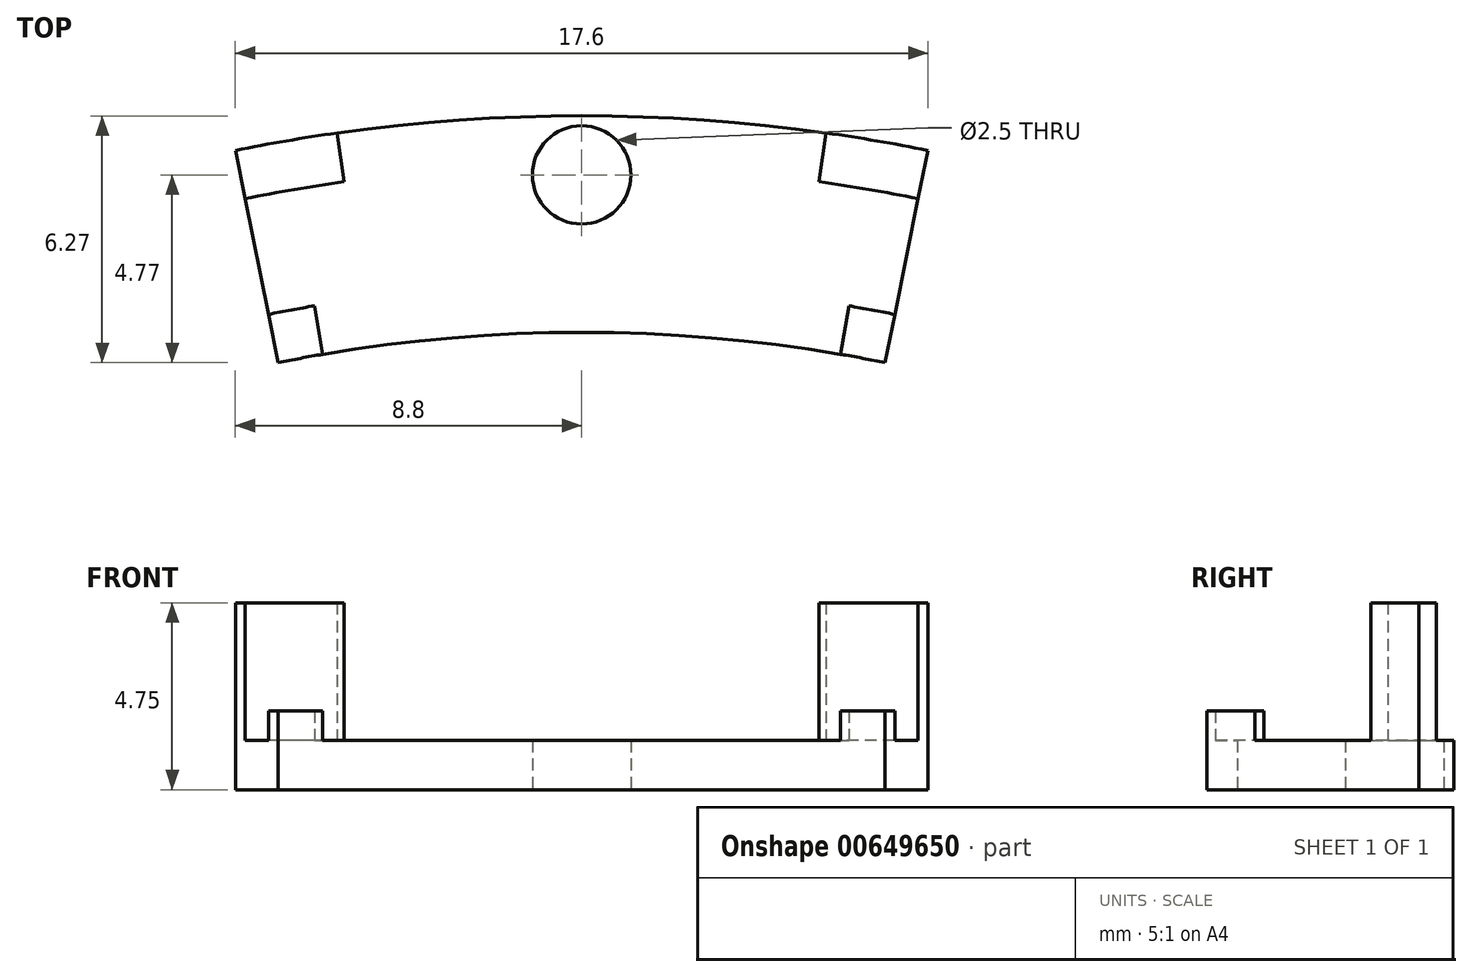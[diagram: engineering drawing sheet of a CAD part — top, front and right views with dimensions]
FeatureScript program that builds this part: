
annotation { "Feature Type Name" : "Feature", "Feature Type Description" : "" }
export const myFeature = defineFeature(function(context is Context, id is Id, definition is map)
    precondition{}
    {
        {
            var Q0;
            Q0=qCreatedBy(makeId("Top.planeOp"),FACE);
            var sketch = newSketch(context, id + "F0", { "sketchPlane" : qUnion([Q0])});
            skCircle(sketch, "E0", {"center": v(0, 0) * mm, "radius": 39 * mm});
            skCircle(sketch, "E1", {"center": v(0, 0) * mm, "radius": 44.5 * mm});
            skCircle(sketch, "E2", {"center": v(0, 43) * mm, "radius": 1.25 * mm});
            skCircle(sketch, "E3", {"center": v(0, 43) * mm, "radius": 6 * mm});
            skLineSegment(sketch, "E4", {"start": v(-7.7, 38.23) * mm, "end": v(-8.8, 43.62) * mm});
            skLineSegment(sketch, "E5", {"start": v(7.7, 38.23) * mm, "end": v(8.8, 43.62) * mm});
            skLineSegment(sketch, "E6", {"start": v(-7.5, 43.86) * mm, "end": v(-6.58, 38.44) * mm});
            skLineSegment(sketch, "E7", {"start": v(6.58, 38.44) * mm, "end": v(7.5, 43.86) * mm});
            skCircle(sketch, "E8", {"center": v(0, 0) * mm, "radius": 40.25 * mm});
            skCircle(sketch, "E9", {"center": v(0, 0) * mm, "radius": 43.25 * mm});
            skSolve(sketch);
        }
        {
            var Q0;
            {var subQ0=sQuery(id+"F0.wireOp",EDGE,"E7");var subQ1=sQuery(id+"F0.wireOp",EDGE,"E1");var subQ2=makeQuery(id+"F0.imprint","INTERSECT",VERTEX,{"derivedFrom":[subQ1,subQ0]});Q0=makeQuery(id+"F0.imprint","IMPRINT",FACE,{"disambiguationData":[TD([[makeQuery(id+"F0.imprint","IMPRINT",EDGE,{"disambiguationData":[TD([[subQ2,-1.0]])],"derivedFrom":subQ1}),1.0]])]});}
            var Q1;
            {var subQ0=sQuery(id+"F0.wireOp",EDGE,"E6");var subQ1=sQuery(id+"F0.wireOp",EDGE,"E1");var subQ2=makeQuery(id+"F0.imprint","INTERSECT",VERTEX,{"derivedFrom":[subQ1,subQ0]});Q1=makeQuery(id+"F0.imprint","IMPRINT",FACE,{"disambiguationData":[TD([[makeQuery(id+"F0.imprint","IMPRINT",EDGE,{"disambiguationData":[TD([[subQ2,1.0]])],"derivedFrom":subQ1}),1.0]])]});}
            var Q2;
            {var subQ0=sQuery(id+"F0.wireOp",EDGE,"E3");var subQ1=sQuery(id+"F0.wireOp",EDGE,"E1");var subQ2=makeQuery(id+"F0.imprint","INTERSECT",VERTEX,{"disambiguationData":[OD(0.0)],"derivedFrom":[subQ1,subQ0]});Q2=makeQuery(id+"F0.imprint","IMPRINT",FACE,{"disambiguationData":[TD([[makeQuery(id+"F0.imprint","IMPRINT",EDGE,{"disambiguationData":[TD([[subQ2,-1.0]])],"derivedFrom":subQ1}),1.0]])]});}
            var Q3;
            {var subQ0=sQuery(id+"F0.wireOp",EDGE,"E8");var subQ1=sQuery(id+"F0.wireOp",EDGE,"E3");var subQ2=makeQuery(id+"F0.imprint","INTERSECT",VERTEX,{"disambiguationData":[OD(1.0)],"derivedFrom":[subQ1,subQ0]});Q3=makeQuery(id+"F0.imprint","IMPRINT",FACE,{"disambiguationData":[TD([[makeQuery(id+"F0.imprint","IMPRINT",EDGE,{"disambiguationData":[TD([[subQ2,-1.0]])],"derivedFrom":subQ1}),-1.0]])]});}
            var Q4;
            {var subQ3=sQuery(id+"F0.wireOp",EDGE,"E9");var subQ5=sQuery(id+"F0.wireOp",EDGE,"E2");var subQ6=makeQuery(id+"F0.imprint","INTERSECT",VERTEX,{"disambiguationData":[OD(0.0)],"derivedFrom":[subQ5,subQ3]});Q4=makeQuery(id+"F0.imprint","IMPRINT",FACE,{"disambiguationData":[TD([[makeQuery(id+"F0.imprint","IMPRINT",EDGE,{"disambiguationData":[TD([[subQ6,1.0]])],"derivedFrom":subQ5}),-1.0]])]});}
            var Q5;
            {var subQ0=sQuery(id+"F0.wireOp",EDGE,"E9");var subQ1=sQuery(id+"F0.wireOp",EDGE,"E3");var subQ2=makeQuery(id+"F0.imprint","INTERSECT",VERTEX,{"disambiguationData":[OD(0.0)],"derivedFrom":[subQ1,subQ0]});Q5=makeQuery(id+"F0.imprint","IMPRINT",FACE,{"disambiguationData":[TD([[makeQuery(id+"F0.imprint","IMPRINT",EDGE,{"disambiguationData":[TD([[subQ2,-1.0]])],"derivedFrom":subQ1}),-1.0]])]});}
            var Q6;
            {var subQ0=sQuery(id+"F0.wireOp",EDGE,"E6");var subQ1=sQuery(id+"F0.wireOp",EDGE,"E0");var subQ2=makeQuery(id+"F0.imprint","INTERSECT",VERTEX,{"derivedFrom":[subQ1,subQ0]});Q6=makeQuery(id+"F0.imprint","IMPRINT",FACE,{"disambiguationData":[TD([[makeQuery(id+"F0.imprint","IMPRINT",EDGE,{"disambiguationData":[TD([[subQ2,1.0]])],"derivedFrom":subQ1}),-1.0]])]});}
            var Q7;
            {var subQ0=sQuery(id+"F0.wireOp",EDGE,"E3");var subQ1=sQuery(id+"F0.wireOp",EDGE,"E0");var subQ2=makeQuery(id+"F0.imprint","INTERSECT",VERTEX,{"disambiguationData":[OD(0.0)],"derivedFrom":[subQ1,subQ0]});Q7=makeQuery(id+"F0.imprint","IMPRINT",FACE,{"disambiguationData":[TD([[makeQuery(id+"F0.imprint","IMPRINT",EDGE,{"disambiguationData":[TD([[subQ2,-1.0]])],"derivedFrom":subQ1}),-1.0]])]});}
            var Q8;
            {var subQ0=sQuery(id+"F0.wireOp",EDGE,"E7");var subQ1=sQuery(id+"F0.wireOp",EDGE,"E0");var subQ2=makeQuery(id+"F0.imprint","INTERSECT",VERTEX,{"derivedFrom":[subQ1,subQ0]});Q8=makeQuery(id+"F0.imprint","IMPRINT",FACE,{"disambiguationData":[TD([[makeQuery(id+"F0.imprint","IMPRINT",EDGE,{"disambiguationData":[TD([[subQ2,-1.0]])],"derivedFrom":subQ1}),-1.0]])]});}
            var Q9;
            {var subQ0=sQuery(id+"F0.wireOp",EDGE,"E8");var subQ1=sQuery(id+"F0.wireOp",EDGE,"E5");var subQ2=makeQuery(id+"F0.imprint","INTERSECT",VERTEX,{"derivedFrom":[subQ1,subQ0]});Q9=makeQuery(id+"F0.imprint","IMPRINT",FACE,{"disambiguationData":[TD([[makeQuery(id+"F0.imprint","IMPRINT",EDGE,{"disambiguationData":[TD([[subQ2,-1.0]])],"derivedFrom":subQ1}),1.0]])]});}
            var Q10;
            {var subQ0=sQuery(id+"F0.wireOp",EDGE,"E8");var subQ1=sQuery(id+"F0.wireOp",EDGE,"E4");var subQ2=makeQuery(id+"F0.imprint","INTERSECT",VERTEX,{"derivedFrom":[subQ1,subQ0]});Q10=makeQuery(id+"F0.imprint","IMPRINT",FACE,{"disambiguationData":[TD([[makeQuery(id+"F0.imprint","IMPRINT",EDGE,{"disambiguationData":[TD([[subQ2,-1.0]])],"derivedFrom":subQ1}),-1.0]])]});}
            extrude(context, id + "F1", {"entities" : qUnion([Q0, Q1, Q2, Q3, Q4, Q5, Q6, Q7, Q8, Q9, Q10]), "depth" : 1.25 * mm, "offsetDistance" : 25 * mm});
        }
        {
            var Q0;
            Q0=qCreatedBy(makeId("Top.planeOp"),FACE);
            var sketch = newSketch(context, id + "F2", { "sketchPlane" : qUnion([Q0])});
            skCircle(sketch, "E10", {"center": v(0, 0) * mm, "radius": 39 * mm});
            skCircle(sketch, "E11", {"center": v(0, 0) * mm, "radius": 44.5 * mm});
            skCircle(sketch, "E12", {"center": v(0, 43) * mm, "radius": 0.85 * mm});
            skCircle(sketch, "E13", {"center": v(0, 43) * mm, "radius": 6 * mm});
            skLineSegment(sketch, "E14", {"start": v(-7.7, 38.23) * mm, "end": v(-8.8, 43.62) * mm});
            skLineSegment(sketch, "E15", {"start": v(7.7, 38.23) * mm, "end": v(8.8, 43.62) * mm});
            skLineSegment(sketch, "E16", {"start": v(-6.2, 44.06) * mm, "end": v(-5.44, 38.62) * mm});
            skLineSegment(sketch, "E17", {"start": v(5.44, 38.62) * mm, "end": v(6.2, 44.06) * mm});
            skCircle(sketch, "E18", {"center": v(0, 0) * mm, "radius": 40.25 * mm});
            skCircle(sketch, "E19", {"center": v(0, 0) * mm, "radius": 43.25 * mm});
            skSolve(sketch);
        }
        {
            var Q0;
            {var subQ0=sQuery(id+"F2.wireOp",EDGE,"E15");var subQ1=sQuery(id+"F2.wireOp",EDGE,"E11");var subQ2=makeQuery(id+"F2.imprint","INTERSECT",VERTEX,{"derivedFrom":[subQ1,subQ0]});Q0=makeQuery(id+"F2.imprint","IMPRINT",FACE,{"disambiguationData":[TD([[makeQuery(id+"F2.imprint","IMPRINT",EDGE,{"disambiguationData":[TD([[subQ2,-1.0]])],"derivedFrom":subQ1}),1.0]])]});}
            var Q1;
            {var subQ0=sQuery(id+"F2.wireOp",EDGE,"E14");var subQ1=sQuery(id+"F2.wireOp",EDGE,"E11");var subQ2=makeQuery(id+"F2.imprint","INTERSECT",VERTEX,{"derivedFrom":[subQ1,subQ0]});Q1=makeQuery(id+"F2.imprint","IMPRINT",FACE,{"disambiguationData":[TD([[makeQuery(id+"F2.imprint","IMPRINT",EDGE,{"disambiguationData":[TD([[subQ2,1.0]])],"derivedFrom":subQ1}),1.0]])]});}
            extrude(context, id + "F3", {"entities" : qUnion([Q0, Q1]), "operationType" : NewBodyOperationType.ADD, "depth" : 4.75 * mm, "offsetDistance" : 25 * mm});
        }
        {
            var Q0;
            Q0=qCreatedBy(makeId("Top.planeOp"),FACE);
            var sketch = newSketch(context, id + "F4", { "sketchPlane" : qUnion([Q0])});
            skCircle(sketch, "E20", {"center": v(0, 0) * mm, "radius": 39 * mm});
            skCircle(sketch, "E21", {"center": v(0, 0) * mm, "radius": 44.5 * mm});
            skCircle(sketch, "E22", {"center": v(0, 43) * mm, "radius": 0.85 * mm});
            skCircle(sketch, "E23", {"center": v(0, 43) * mm, "radius": 6 * mm});
            skLineSegment(sketch, "E24", {"start": v(-7.7, 38.23) * mm, "end": v(-8.8, 43.62) * mm});
            skLineSegment(sketch, "E25", {"start": v(7.7, 38.23) * mm, "end": v(8.8, 43.62) * mm});
            skLineSegment(sketch, "E26", {"start": v(-7.5, 43.86) * mm, "end": v(-6.58, 38.44) * mm});
            skLineSegment(sketch, "E27", {"start": v(6.58, 38.44) * mm, "end": v(7.5, 43.86) * mm});
            skCircle(sketch, "E28", {"center": v(0, 0) * mm, "radius": 40.25 * mm});
            skCircle(sketch, "E29", {"center": v(0, 0) * mm, "radius": 43.25 * mm});
            skSolve(sketch);
        }
        {
            var Q0;
            {var subQ0=sQuery(id+"F4.wireOp",EDGE,"E24");var subQ1=sQuery(id+"F4.wireOp",EDGE,"E20");var subQ2=makeQuery(id+"F4.imprint","INTERSECT",VERTEX,{"derivedFrom":[subQ1,subQ0]});Q0=makeQuery(id+"F4.imprint","IMPRINT",FACE,{"disambiguationData":[TD([[makeQuery(id+"F4.imprint","IMPRINT",EDGE,{"disambiguationData":[TD([[subQ2,1.0]])],"derivedFrom":subQ1}),-1.0]])]});}
            var Q1;
            {var subQ0=sQuery(id+"F4.wireOp",EDGE,"E25");var subQ1=sQuery(id+"F4.wireOp",EDGE,"E20");var subQ2=makeQuery(id+"F4.imprint","INTERSECT",VERTEX,{"derivedFrom":[subQ1,subQ0]});Q1=makeQuery(id+"F4.imprint","IMPRINT",FACE,{"disambiguationData":[TD([[makeQuery(id+"F4.imprint","IMPRINT",EDGE,{"disambiguationData":[TD([[subQ2,-1.0]])],"derivedFrom":subQ1}),-1.0]])]});}
            extrude(context, id + "F5", {"entities" : qUnion([Q0, Q1]), "operationType" : NewBodyOperationType.ADD, "depth" : 2 * mm, "offsetDistance" : 25 * mm});
        }
    });
